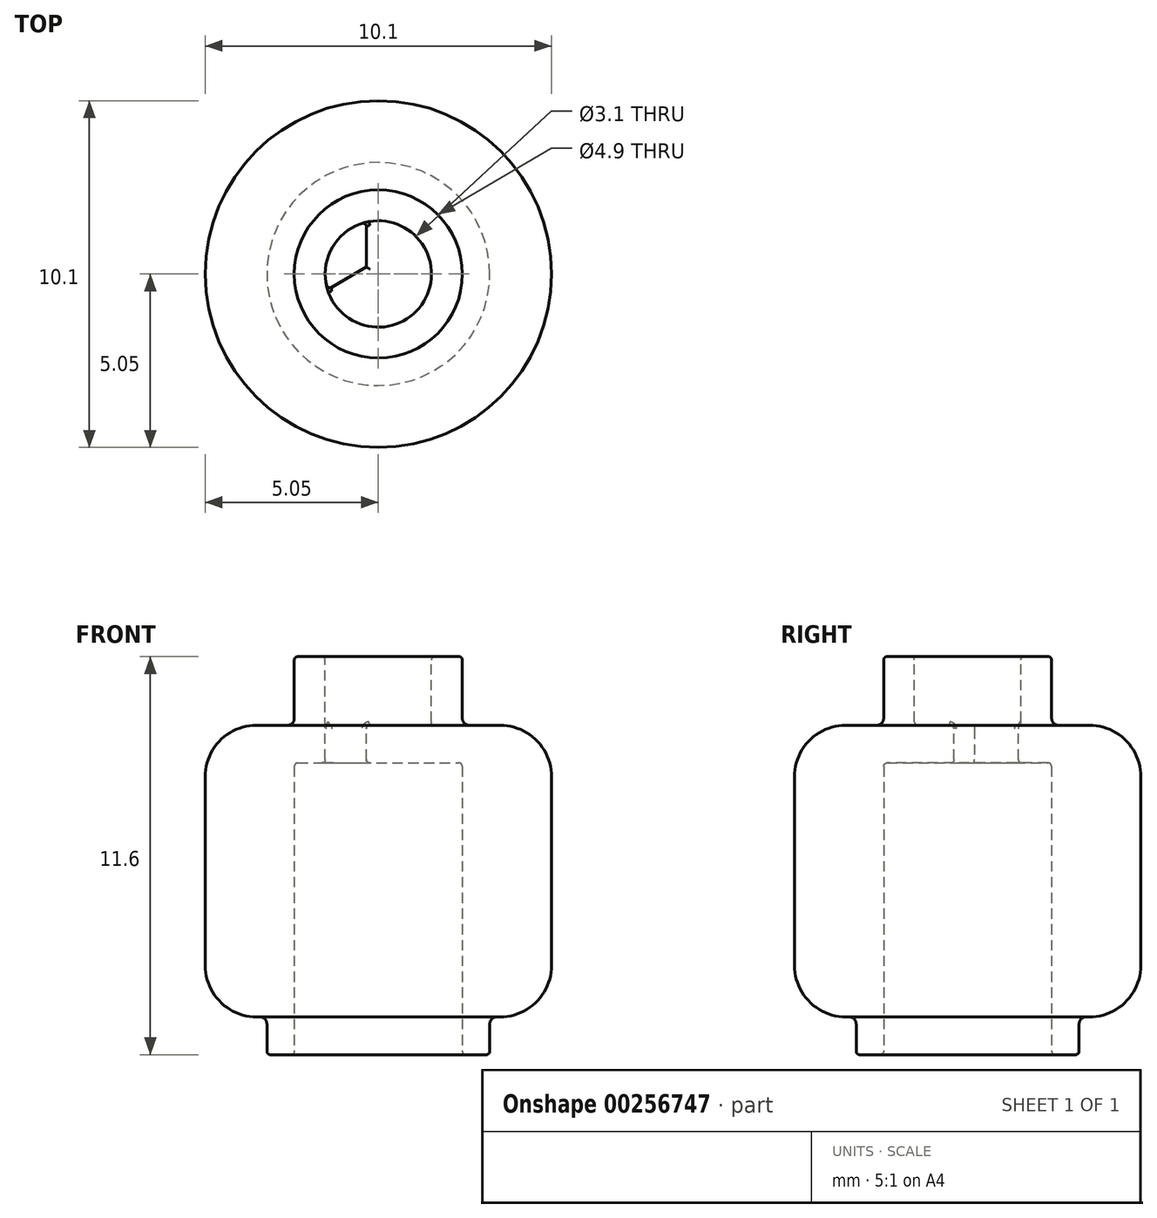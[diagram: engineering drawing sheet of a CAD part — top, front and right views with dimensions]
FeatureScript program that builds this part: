
annotation { "Feature Type Name" : "Feature", "Feature Type Description" : "" }
export const myFeature = defineFeature(function(context is Context, id is Id, definition is map)
    precondition{}
    {
        {
            var Q0;
            Q0=qCreatedBy(makeId("Front.planeOp"),FACE);
            var sketch = newSketch(context, id + "F0", { "sketchPlane" : qUnion([Q0])});
            skLineSegment(sketch, "E0", {"start": v(0, 5.8) * mm, "end": v(0, -5.8) * mm});
            skLineSegment(sketch, "E1", {"start": v(0, -5.8) * mm, "end": v(-3.25, -5.8) * mm});
            skLineSegment(sketch, "E2", {"start": v(-3.25, -5.8) * mm, "end": v(-3.25, -4.7) * mm});
            skLineSegment(sketch, "E3", {"start": v(-3.25, -4.7) * mm, "end": v(-5.05, -4.7) * mm});
            skLineSegment(sketch, "E4", {"start": v(-5.05, -4.7) * mm, "end": v(-5.05, 3.8) * mm});
            skLineSegment(sketch, "E5", {"start": v(-5.05, 3.8) * mm, "end": v(-2.45, 3.8) * mm});
            skLineSegment(sketch, "E6", {"start": v(-2.45, 3.8) * mm, "end": v(-2.45, 5.8) * mm});
            skLineSegment(sketch, "E7", {"start": v(-2.45, 5.8) * mm, "end": v(0, 5.8) * mm});
            skPoint(sketch, "E8", {"position": v(0, 0) * mm});
            skSolve(sketch);
        }
        {
            var Q0;
            Q0=makeQuery(id+"F0.imprint","IMPRINT",FACE,{"disambiguationData":[TD([[makeQuery(id+"F0.imprint","IMPRINT",EDGE,{"derivedFrom":sQuery(id+"F0.wireOp",EDGE,"E0")}),-1.0]])]});
            var Q1;
            Q1=sQuery(id+"F0.wireOp",EDGE,"E0");
            revolve(context, id + "F1", {"entities" : qUnion([Q0]), "axis" : qUnion([Q1]), "revolveType" : RevolveType.FULL});
        }
        {
            var Q0;
            Q0=makeQuery(id+"F1.opRevolve","SWEPT_EDGE",EDGE,{"disambiguationData":[OSD([sQuery(id+"F0.wireOp",EDGE,"E4"),sQuery(id+"F0.wireOp",EDGE,"E5")])]});
            var Q1;
            Q1=makeQuery(id+"F1.opRevolve","SWEPT_EDGE",EDGE,{"disambiguationData":[OSD([sQuery(id+"F0.wireOp",EDGE,"E3"),sQuery(id+"F0.wireOp",EDGE,"E4")])]});
            fillet(context, id + "F2", {"entities" : qUnion([Q0, Q1]), "radius" : 1.5 * mm, "tangentPropagation" : true, "allowEdgeOverflow" : false});
        }
        {
            var Q0;
            Q0=makeQuery(id+"F1.opRevolve","SWEPT_FACE",FACE,{"disambiguationData":[OSD([sQuery(id+"F0.wireOp",EDGE,"E7")])]});
            var sketch = newSketch(context, id + "F3", { "sketchPlane" : qUnion([Q0])});
            skCircle(sketch, "E9", {"center": v(0, 0) * mm, "radius": 1.55 * mm});
            skSolve(sketch);
        }
        {
            var Q0;
            Q0=makeQuery(id+"F3.imprint","IMPRINT",FACE,{"disambiguationData":[TD([[makeQuery(id+"F3.imprint","IMPRINT",EDGE,{"derivedFrom":sQuery(id+"F3.wireOp",EDGE,"E9")}),1.0]])]});
            var Q1;
            Q1=makeQuery(id+"F1.opRevolve","SWEPT_FACE",FACE,{"disambiguationData":[OSD([sQuery(id+"F0.wireOp",EDGE,"E5")])]});
            extrude(context, id + "F4", {"entities" : qUnion([Q0]), "operationType" : NewBodyOperationType.REMOVE, "endBound" : BoundingType.UP_TO_SURFACE, "oppositeDirection" : true, "endBoundEntityFace" : qUnion([Q1]), "depth" : 25 * mm});
        }
        {
            var Q0;
            Q0=makeQuery(id+"F1.opRevolve","SWEPT_FACE",FACE,{"disambiguationData":[OSD([sQuery(id+"F0.wireOp",EDGE,"E1")])]});
            var sketch = newSketch(context, id + "F5", { "sketchPlane" : qUnion([Q0])});
            skCircle(sketch, "E10", {"center": v(0, 0) * mm, "radius": 2.45 * mm});
            skSolve(sketch);
        }
        {
            var Q0;
            Q0=makeQuery(id+"F5.imprint","IMPRINT",FACE,{"disambiguationData":[TD([[makeQuery(id+"F5.imprint","IMPRINT",EDGE,{"derivedFrom":sQuery(id+"F5.wireOp",EDGE,"E10")}),1.0]])]});
            extrude(context, id + "F6", {"entities" : qUnion([Q0]), "operationType" : NewBodyOperationType.REMOVE, "oppositeDirection" : true, "depth" : 8.5 * mm});
        }
        {
            var Q0;
            Q0=makeQuery(id+"F1.opRevolve","SWEPT_EDGE",EDGE,{"disambiguationData":[OSD([sQuery(id+"F0.wireOp",EDGE,"E6"),sQuery(id+"F0.wireOp",EDGE,"E7")])]});
            var Q1;
            Q1=makeQuery(id+"F4.boolean.opBoolean","COPY",EDGE,{"derivedFrom":makeQuery(id+"F4.opExtrude","CAP_EDGE",EDGE,{"disambiguationData":[OSD([sQuery(id+"F3.wireOp",EDGE,"E9")])],"isStart":true})});
            var Q2;
            Q2=makeQuery(id+"F1.opRevolve","SWEPT_FACE",FACE,{"disambiguationData":[OSD([sQuery(id+"F0.wireOp",EDGE,"E1")])]});
            fillet(context, id + "F7", {"entities" : qUnion([Q0, Q1, Q2]), "radius" : 0.1 * mm, "tangentPropagation" : true, "allowEdgeOverflow" : false});
        }
        {
            var Q0;
            Q0=makeQuery(id+"F1.opRevolve","SWEPT_EDGE",EDGE,{"disambiguationData":[OSD([sQuery(id+"F0.wireOp",EDGE,"E5"),sQuery(id+"F0.wireOp",EDGE,"E6")])]});
            var Q1;
            Q1=makeQuery(id+"F1.opRevolve","SWEPT_EDGE",EDGE,{"disambiguationData":[OSD([sQuery(id+"F0.wireOp",EDGE,"E2"),sQuery(id+"F0.wireOp",EDGE,"E3")])]});
            fillet(context, id + "F8", {"entities" : qUnion([Q0, Q1]), "radius" : 0.2 * mm, "tangentPropagation" : true, "allowEdgeOverflow" : false});
        }
        {
            var Q0;
            Q0=qCreatedBy(makeId("Top.planeOp"),FACE);
            var sketch = newSketch(context, id + "F9", { "sketchPlane" : qUnion([Q0])});
            skArc(sketch, "E11", {"start": v(-0.35, 1.5) * mm, "mid": v(-1.34, 0.78) * mm, "end": v(-1.48, -0.45) * mm});
            skLineSegment(sketch, "E12", {"start": v(-0.35, 0.2) * mm, "end": v(-0.35, 1.5) * mm});
            skLineSegment(sketch, "E13", {"start": v(-1.48, -0.45) * mm, "end": v(-0.35, 0.2) * mm});
            skSolve(sketch);
        }
        {
            var Q0;
            Q0 = qSketchRegion(id + "F9", true);
            extrude(context, id + "F10", {"entities" : qUnion([Q0]), "operationType" : NewBodyOperationType.REMOVE, "depth" : 25 * mm, "symmetric" : true});
        }
        {
            var Q0;
            {var subQ0=sQuery(id+"F9.wireOp",EDGE,"E11");Q0=makeQuery(id+"Fkj9d5jUecSIw6N_1.2.F10.boolean.opBoolean","MERGE",FACE,{"derivedFrom":[makeQuery(id+"Fkj9d5jUecSIw6N_1.1.F10.boolean.opBoolean","MERGE",FACE,{"derivedFrom":[makeQuery(id+"F10.boolean.opBoolean","MERGE",FACE,{"derivedFrom":[makeQuery(id+"F4.boolean.opBoolean","COPY",FACE,{"derivedFrom":makeQuery(id+"F4.opExtrude","SWEPT_FACE",FACE,{"disambiguationData":[OSD([sQuery(id+"F3.wireOp",EDGE,"E9")])]})})],"fromTools":[makeQuery(id+"F10.opExtrude","SWEPT_FACE",FACE,{"disambiguationData":[OSD([subQ0])]})]})],"fromTools":[makeQuery(id+"Fkj9d5jUecSIw6N_1.1.F10.opExtrude","SWEPT_FACE",FACE,{"disambiguationData":[OSD([subQ0])]})]})],"fromTools":[makeQuery(id+"Fkj9d5jUecSIw6N_1.2.F10.opExtrude","SWEPT_FACE",FACE,{"disambiguationData":[OSD([subQ0])]})]});}
            var Q1;
            Q1=makeQuery(id+"F4.boolean.opBoolean","COPY",FACE,{"derivedFrom":makeQuery(id+"F4.opExtrude","CAP_FACE",FACE,{"disambiguationData":[OSD([sQuery(id+"F3.wireOp",EDGE,"E9")])],"isStart":false})});
            var Q2;
            Q2=makeQuery(id+"F6.boolean.opBoolean","COPY",FACE,{"derivedFrom":makeQuery(id+"F6.opExtrude","CAP_FACE",FACE,{"disambiguationData":[OSD([sQuery(id+"F5.wireOp",EDGE,"E10")])],"isStart":false})});
            fillet(context, id + "F11", {"entities" : qUnion([Q0, Q1, Q2]), "radius" : 0.1 * mm, "tangentPropagation" : true, "allowEdgeOverflow" : false});
        }
    });
